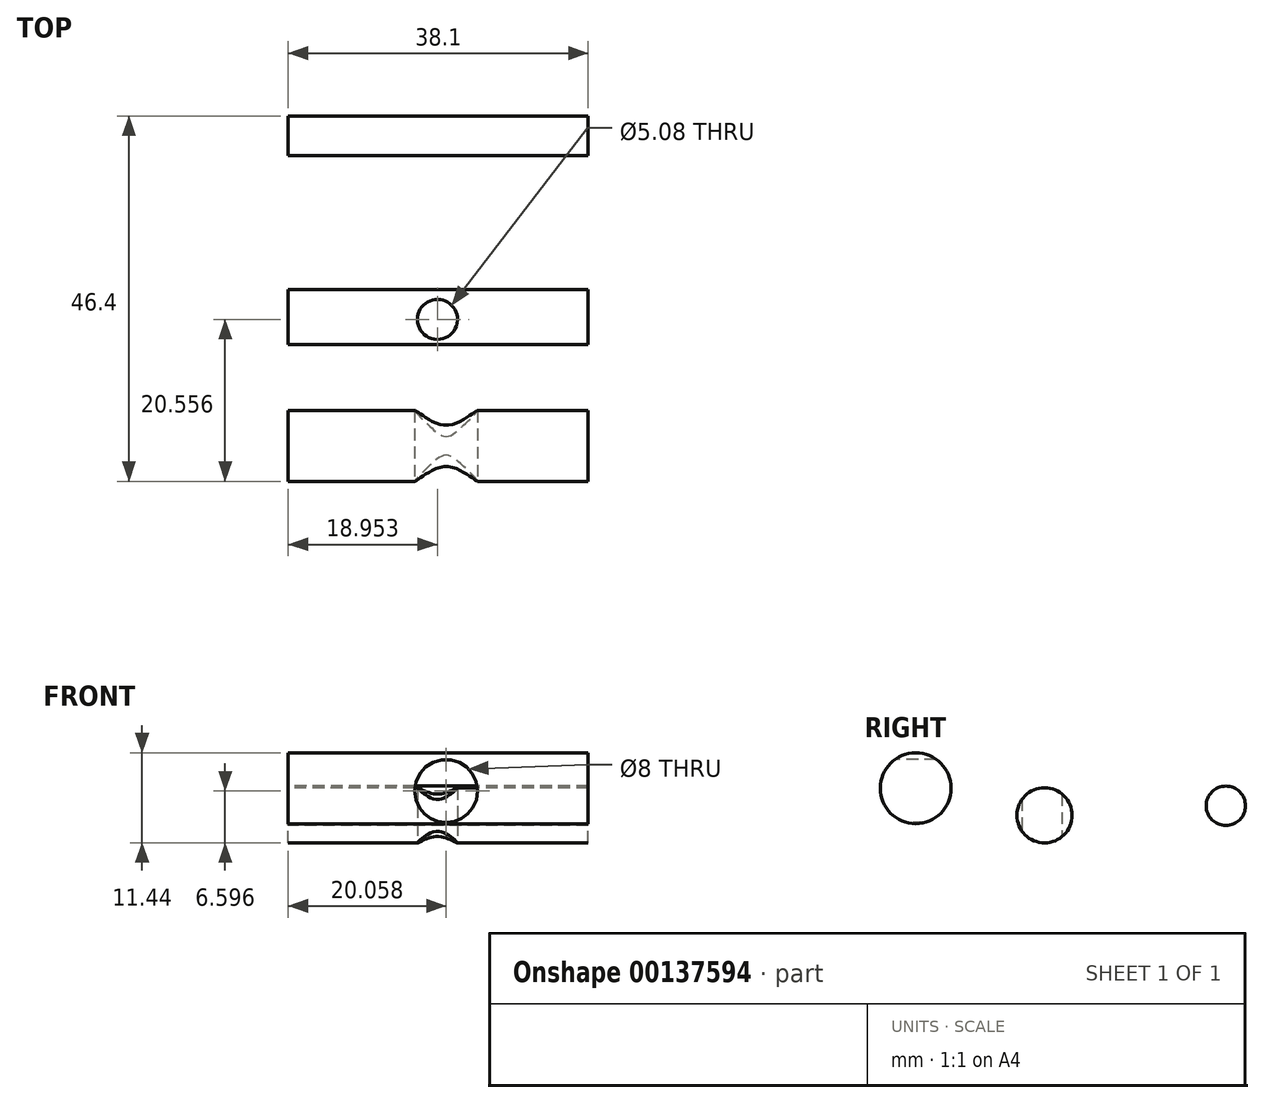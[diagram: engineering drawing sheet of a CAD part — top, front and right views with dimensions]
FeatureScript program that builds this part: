
annotation { "Feature Type Name" : "Feature", "Feature Type Description" : "" }
export const myFeature = defineFeature(function(context is Context, id is Id, definition is map)
    precondition{}
    {
        {
            var Q0;
            Q0=qCreatedBy(makeId("Right.planeOp"),FACE);
            var sketch = newSketch(context, id + "F0", { "sketchPlane" : qUnion([Q0])});
            skCircle(sketch, "E0", {"center": v(55.06, 26.27) * mm, "radius": 2.5 * mm});
            skCircle(sketch, "E1", {"center": v(32.02, 25.05) * mm, "radius": 3.5 * mm});
            skCircle(sketch, "E2", {"center": v(15.66, 28.49) * mm, "radius": 4.5 * mm});
            skSolve(sketch);
        }
        {
            var Q0;
            Q0=makeQuery(id+"F0.imprint","IMPRINT",FACE,{"disambiguationData":[TD([[makeQuery(id+"F0.imprint","IMPRINT",EDGE,{"derivedFrom":sQuery(id+"F0.wireOp",EDGE,"E1")}),1.0]])]});
            var Q1;
            Q1=makeQuery(id+"F0.imprint","IMPRINT",FACE,{"disambiguationData":[TD([[makeQuery(id+"F0.imprint","IMPRINT",EDGE,{"derivedFrom":sQuery(id+"F0.wireOp",EDGE,"E0")}),1.0]])]});
            var Q2;
            Q2=makeQuery(id+"F0.imprint","IMPRINT",FACE,{"disambiguationData":[TD([[makeQuery(id+"F0.imprint","IMPRINT",EDGE,{"derivedFrom":sQuery(id+"F0.wireOp",EDGE,"E2")}),1.0]])]});
            var Q3;
            Q3=sQuery(id+"F0.wireOp",EDGE,"E1");
            var Q4;
            Q4=sQuery(id+"F0.wireOp",EDGE,"E0");
            var Q5;
            Q5=sQuery(id+"F0.wireOp",EDGE,"E2");
            extrude(context, id + "F1", {"entities" : qUnion([Q0, Q1, Q2]), "surfaceEntities" : qUnion([Q3, Q4, Q5]), "depth" : 38.1 * mm});
        }
        {
            var Q0;
            Q0=qCreatedBy(makeId("Front.planeOp"),FACE);
            var sketch = newSketch(context, id + "F2", { "sketchPlane" : qUnion([Q0])});
            skCircle(sketch, "E3", {"center": v(20.06, 28.15) * mm, "radius": 4 * mm});
            skSolve(sketch);
        }
        {
            var Q0;
            Q0=makeQuery(id+"F2.imprint","IMPRINT",FACE,{"disambiguationData":[TD([[makeQuery(id+"F2.imprint","IMPRINT",EDGE,{"derivedFrom":sQuery(id+"F2.wireOp",EDGE,"E3")}),1.0]])]});
            extrude(context, id + "F3", {"entities" : qUnion([Q0]), "operationType" : NewBodyOperationType.REMOVE, "oppositeDirection" : true, "depth" : 24.76 * mm});
        }
        {
            var Q0;
            Q0=qCreatedBy(makeId("Top.planeOp"),FACE);
            var sketch = newSketch(context, id + "F4", { "sketchPlane" : qUnion([Q0])});
            skCircle(sketch, "E4", {"center": v(18.95, 31.72) * mm, "radius": 2.54 * mm});
            skSolve(sketch);
        }
        {
            var Q0;
            Q0 = qSketchRegion(id + "F4", true);
            extrude(context, id + "F5", {"entities" : qUnion([Q0]), "operationType" : NewBodyOperationType.REMOVE, "endBound" : BoundingType.THROUGH_ALL, "depth" : 25.4 * mm});
        }
    });
